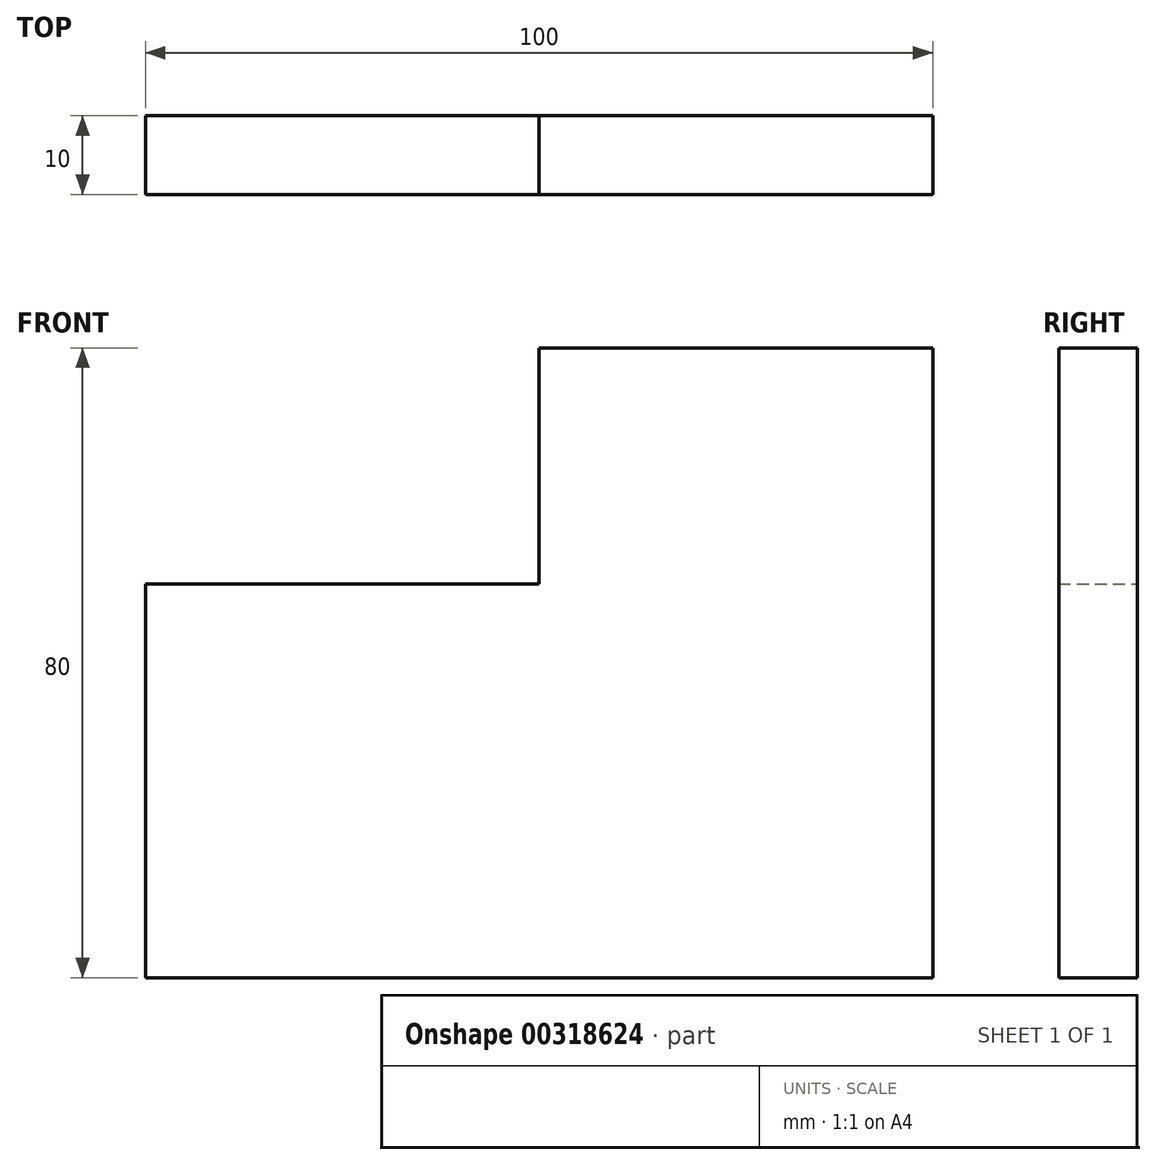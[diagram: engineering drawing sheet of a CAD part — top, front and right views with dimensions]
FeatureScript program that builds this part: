
annotation { "Feature Type Name" : "Feature", "Feature Type Description" : "" }
export const myFeature = defineFeature(function(context is Context, id is Id, definition is map)
    precondition{}
    {
        {
            var Q0;
            Q0=qCreatedBy(makeId("Front.planeOp"),FACE);
            var sketch = newSketch(context, id + "F0", { "sketchPlane" : qUnion([Q0])});
            skLineSegment(sketch, "E0", {"start": v(0, 0) * mm, "end": v(0, 80) * mm});
            skLineSegment(sketch, "E1", {"start": v(0, 80) * mm, "end": v(-50, 80) * mm});
            skLineSegment(sketch, "E2", {"start": v(-50, 80) * mm, "end": v(-50, 50) * mm});
            skLineSegment(sketch, "E3", {"start": v(-50, 50) * mm, "end": v(-100, 50) * mm});
            skLineSegment(sketch, "E4", {"start": v(-100, 50) * mm, "end": v(-100, 0) * mm});
            skLineSegment(sketch, "E5", {"start": v(0, 0) * mm, "end": v(-100, 0) * mm});
            skSolve(sketch);
        }
        {
            var Q0;
            Q0=makeQuery(id+"F0.imprint","IMPRINT",FACE,{"disambiguationData":[TD([[makeQuery(id+"F0.imprint","IMPRINT",EDGE,{"derivedFrom":sQuery(id+"F0.wireOp",EDGE,"E0")}),1.0]])]});
            extrude(context, id + "F1", {"entities" : qUnion([Q0]), "depth" : 10 * mm});
        }
    });
